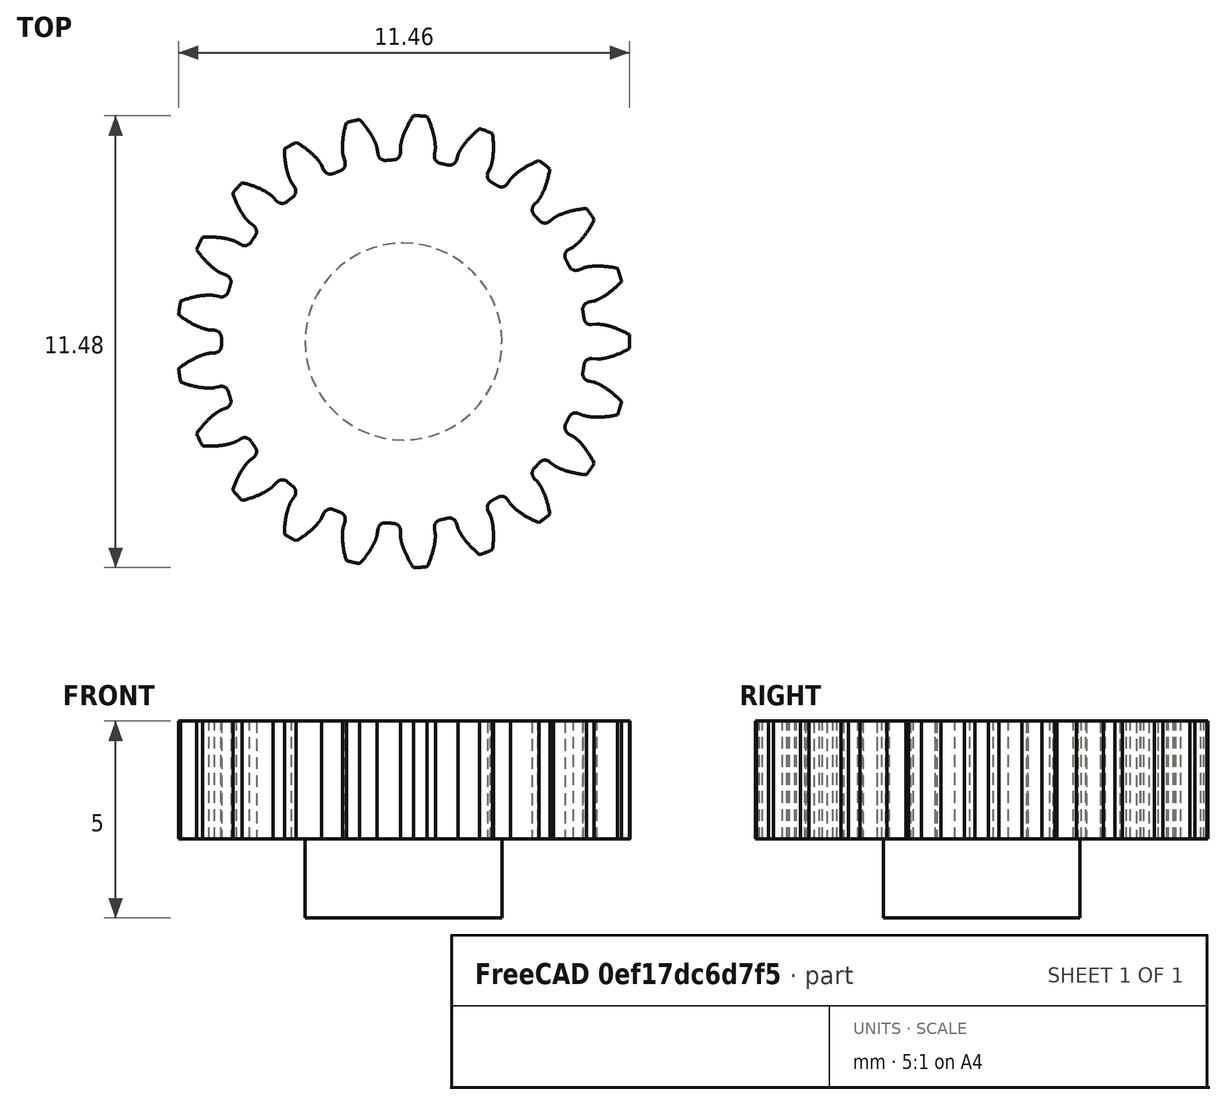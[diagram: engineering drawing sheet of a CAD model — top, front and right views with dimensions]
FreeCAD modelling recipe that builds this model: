
FCSTD DOCUMENT  (FreeCAD 0.17R13541 (Git))
Label: laser_sledge__driving_gear
License: All rights reserved
LicenseURL: http://en.wikipedia.org/wiki/All_rights_reserved
objects: PartDesign::Pad×2, Part::Part2DObjectPython×1, Sketcher::SketchObject×1, PartDesign::Body×1
note: 7 computed .brp shape members not serialized (recipe doc carries the construction recipe); baked Part::Feature solids carry a one-line shape summary decoded from their .brp

FEATURE [Part::Part2DObjectPython] InvoluteGear  # Draft 2D object (typed FeaturePython)
  ExternalGear = true
  HighPrecision = true
  Modules = 0.5
  NumberOfTeeth = 21
  PressureAngle = 20
FEATURE [Sketcher::SketchObject] Sketch
  MapMode = 5
  Support = -> [XY_Plane]
  sketch-geometry (1):
    g0: Circle CenterX=0 CenterY=0 CenterZ=0 NormalX=0 NormalY=0 NormalZ=1 AngleXU=0 Radius=2.5
  constraints (2):
    c: Coincident(g0,g-1)
    c: Radius(g0) = 2.5
FEATURE [PartDesign::Pad] Pad
  Length = 3
  Length2 = 100
  Profile = -> InvoluteGear
  Type = 0
FEATURE [PartDesign::Pad] Pad001
  BaseFeature = -> Pad
  Length = 2
  Length2 = 100
  Profile = -> Sketch
  Reversed = true
  Type = 0
FEATURE [PartDesign::Body] Body
  Group = -> [Sketch,InvoluteGear,Pad,Pad001]
  Origin = -> Origin
  Tip = -> Pad001
